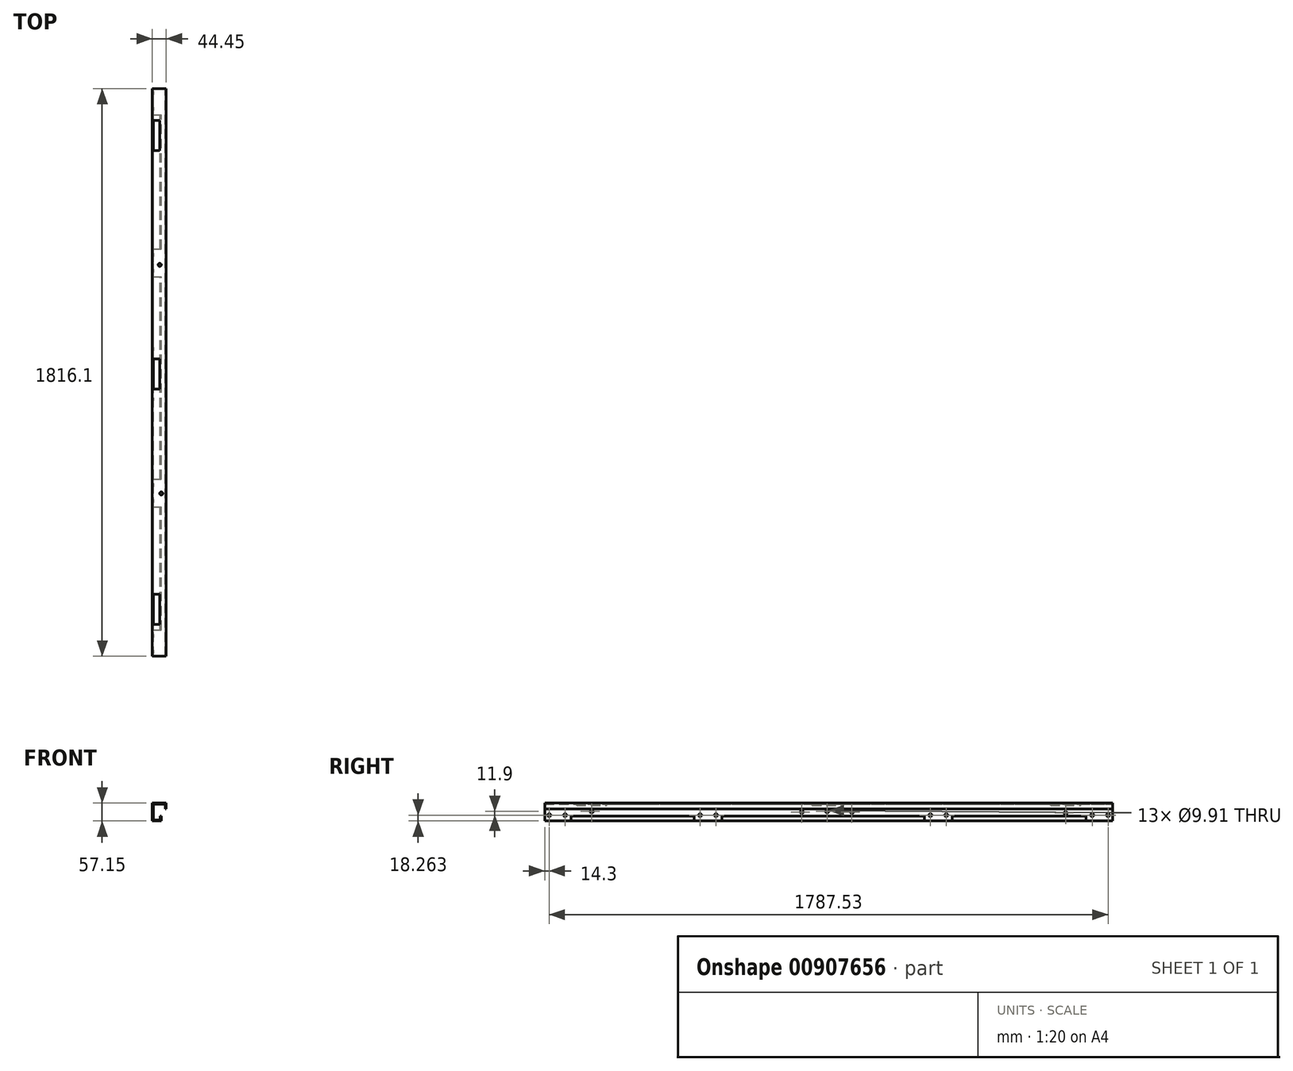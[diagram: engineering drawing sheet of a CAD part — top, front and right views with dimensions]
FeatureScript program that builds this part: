
annotation { "Feature Type Name" : "Feature", "Feature Type Description" : "" }
export const myFeature = defineFeature(function(context is Context, id is Id, definition is map)
    precondition{}
    {
        {
            var Q0;
            Q0=qCreatedBy(makeId("Front.planeOp"),FACE);
            var sketch = newSketch(context, id + "F0", { "sketchPlane" : qUnion([Q0])});
            skLineSegment(sketch, "E0", {"start": v(0, 0) * mm, "end": v(44.45, 0) * mm});
            skLineSegment(sketch, "E1", {"start": v(44.45, 0) * mm, "end": v(44.45, -19.05) * mm});
            skLineSegment(sketch, "E2", {"start": v(0, 0) * mm, "end": v(0, -57.15) * mm});
            skLineSegment(sketch, "E3", {"start": v(0, -57.15) * mm, "end": v(28.58, -57.15) * mm});
            skLineSegment(sketch, "E4", {"start": v(3.3, -53.85) * mm, "end": v(3.3, -3.3) * mm});
            skLineSegment(sketch, "E5", {"start": v(3.3, -3.3) * mm, "end": v(41.15, -3.3) * mm});
            skLineSegment(sketch, "E6", {"start": v(41.15, -3.3) * mm, "end": v(41.15, -19.05) * mm});
            skLineSegment(sketch, "E7", {"start": v(44.45, -19.05) * mm, "end": v(41.15, -19.05) * mm});
            skLineSegment(sketch, "E8", {"start": v(28.58, -41.27) * mm, "end": v(28.58, -57.15) * mm});
            skLineSegment(sketch, "E9", {"start": v(28.58, -41.27) * mm, "end": v(25.27, -41.27) * mm});
            skLineSegment(sketch, "E10", {"start": v(25.27, -41.27) * mm, "end": v(25.27, -53.85) * mm});
            skLineSegment(sketch, "E11", {"start": v(25.27, -53.85) * mm, "end": v(3.3, -53.85) * mm});
            skSolve(sketch);
        }
        {
            var Q0;
            Q0 = qSketchRegion(id + "F0", true);
            extrude(context, id + "F1", {"entities" : qUnion([Q0]), "depth" : 1816.1 * mm, "offsetDistance" : 25.4 * mm});
        }
        {
            var Q0;
            Q0=makeQuery(id+"F1.opExtrude","SWEPT_FACE",FACE,{"disambiguationData":[OSD([sQuery(id+"F0.wireOp",EDGE,"E0")])]});
            var sketch = newSketch(context, id + "F2", { "sketchPlane" : qUnion([Q0])});
            skCircle(sketch, "E12", {"center": v(23.62, -563.75) * mm, "radius": 4.95 * mm});
            skCircle(sketch, "E13", {"center": v(28.58, -1295.4) * mm, "radius": 4.97 * mm});
            skSolve(sketch);
        }
        {
            var Q0;
            Q0 = qSketchRegion(id + "F2", true);
            extrude(context, id + "F3", {"entities" : qUnion([Q0]), "operationType" : NewBodyOperationType.REMOVE, "oppositeDirection" : true, "depth" : 25.4 * mm, "offsetDistance" : 25.4 * mm});
        }
        {
            var Q0;
            Q0=makeQuery(id+"F1.opExtrude","SWEPT_FACE",FACE,{"disambiguationData":[OSD([sQuery(id+"F0.wireOp",EDGE,"E2")])]});
            var sketch = newSketch(context, id + "F4", { "sketchPlane" : qUnion([Q0])});
            skCircle(sketch, "E14", {"center": v(14.27, -38.89) * mm, "radius": 4.95 * mm});
            skCircle(sketch, "E15", {"center": v(65.07, -38.89) * mm, "radius": 4.95 * mm});
            skCircle(sketch, "E16", {"center": v(531.8, -38.89) * mm, "radius": 4.95 * mm});
            skCircle(sketch, "E17", {"center": v(582.6, -38.89) * mm, "radius": 4.95 * mm});
            skCircle(sketch, "E18", {"center": v(1268.4, -38.89) * mm, "radius": 4.95 * mm});
            skCircle(sketch, "E19", {"center": v(1319.2, -38.89) * mm, "radius": 4.95 * mm});
            skCircle(sketch, "E20", {"center": v(1751, -38.89) * mm, "radius": 4.95 * mm});
            skCircle(sketch, "E21", {"center": v(1801.8, -38.89) * mm, "radius": 4.95 * mm});
            skSolve(sketch);
        }
        {
            var Q0;
            Q0 = qSketchRegion(id + "F4", true);
            extrude(context, id + "F5", {"entities" : qUnion([Q0]), "operationType" : NewBodyOperationType.REMOVE, "oppositeDirection" : true, "depth" : 25.4 * mm, "offsetDistance" : 25.4 * mm});
        }
        {
            var Q0;
            Q0=makeQuery(id+"F1.opExtrude","SWEPT_FACE",FACE,{"disambiguationData":[OSD([sQuery(id+"F0.wireOp",EDGE,"E2")])]});
            var sketch = newSketch(context, id + "F6", { "sketchPlane" : qUnion([Q0])});
            skCircle(sketch, "E22", {"center": v(833.44, -28.58) * mm, "radius": 4.95 * mm});
            skCircle(sketch, "E23", {"center": v(993.78, -28.58) * mm, "radius": 4.95 * mm});
            skSolve(sketch);
        }
        {
            var Q0;
            Q0 = qSketchRegion(id + "F6", true);
            extrude(context, id + "F7", {"entities" : qUnion([Q0]), "operationType" : NewBodyOperationType.REMOVE, "oppositeDirection" : true, "depth" : 25.4 * mm, "offsetDistance" : 25.4 * mm});
        }
        {
            var Q0;
            Q0=makeQuery(id+"F1.opExtrude","SWEPT_FACE",FACE,{"disambiguationData":[OSD([sQuery(id+"F0.wireOp",EDGE,"E0")])]});
            var sketch = newSketch(context, id + "F8", { "sketchPlane" : qUnion([Q0])});
            skLineSegment(sketch, "E24.bottom", {"start": v(0, -101.6) * mm, "end": v(23.93, -101.6) * mm});
            skLineSegment(sketch, "E24.top", {"start": v(0, -198.44) * mm, "end": v(23.93, -198.44) * mm});
            skLineSegment(sketch, "E24.left", {"start": v(0, -101.6) * mm, "end": v(0, -198.44) * mm});
            skLineSegment(sketch, "E24.right", {"start": v(23.93, -101.6) * mm, "end": v(23.93, -198.44) * mm});
            skLineSegment(sketch, "E25.bottom", {"start": v(0, -1714.5) * mm, "end": v(24.13, -1714.5) * mm});
            skLineSegment(sketch, "E25.top", {"start": v(0, -1617.66) * mm, "end": v(24.13, -1617.66) * mm});
            skLineSegment(sketch, "E25.left", {"start": v(0, -1714.5) * mm, "end": v(0, -1617.66) * mm});
            skLineSegment(sketch, "E25.right", {"start": v(24.13, -1714.5) * mm, "end": v(24.13, -1617.66) * mm});
            skLineSegment(sketch, "E26.bottom", {"start": v(0, -961.22) * mm, "end": v(24.13, -961.22) * mm});
            skLineSegment(sketch, "E26.top", {"start": v(0, -864.39) * mm, "end": v(24.13, -864.39) * mm});
            skLineSegment(sketch, "E26.left", {"start": v(0, -961.22) * mm, "end": v(0, -864.39) * mm});
            skLineSegment(sketch, "E26.right", {"start": v(24.13, -961.22) * mm, "end": v(24.13, -864.39) * mm});
            skSolve(sketch);
        }
        {
            var Q0;
            Q0 = qSketchRegion(id + "F8", true);
            extrude(context, id + "F9", {"entities" : qUnion([Q0]), "operationType" : NewBodyOperationType.REMOVE, "oppositeDirection" : true, "depth" : 7.62 * mm, "offsetDistance" : 25.4 * mm});
        }
        {
            var Q0;
            Q0=makeQuery(id+"F1.opExtrude","SWEPT_FACE",FACE,{"disambiguationData":[OSD([sQuery(id+"F0.wireOp",EDGE,"E2")])]});
            var sketch = newSketch(context, id + "F10", { "sketchPlane" : qUnion([Q0])});
            skCircle(sketch, "E27", {"center": v(150.03, -31.94) * mm, "radius": 4.95 * mm});
            skCircle(sketch, "E28", {"center": v(912.81, -26.99) * mm, "radius": 4.95 * mm});
            skCircle(sketch, "E29", {"center": v(1666.09, -26.99) * mm, "radius": 4.95 * mm});
            skSolve(sketch);
        }
        {
            var Q0;
            Q0 = qSketchRegion(id + "F10", true);
            extrude(context, id + "F11", {"entities" : qUnion([Q0]), "operationType" : NewBodyOperationType.REMOVE, "oppositeDirection" : true, "depth" : 25.4 * mm, "offsetDistance" : 25.4 * mm});
        }
        {
            var Q0;
            Q0=makeQuery(id+"F1.opExtrude","SWEPT_FACE",FACE,{"disambiguationData":[OSD([sQuery(id+"F0.wireOp",EDGE,"E8")])]});
            var sketch = newSketch(context, id + "F12", { "sketchPlane" : qUnion([Q0])});
            skLineSegment(sketch, "E30.bottom", {"start": v(-1816.1, -57.15) * mm, "end": v(-1731.95, -57.15) * mm});
            skLineSegment(sketch, "E30.top", {"start": v(-1816.1, -41.27) * mm, "end": v(-1731.95, -41.27) * mm});
            skLineSegment(sketch, "E30.left", {"start": v(-1816.1, -57.15) * mm, "end": v(-1816.1, -41.27) * mm});
            skLineSegment(sketch, "E30.right", {"start": v(-1731.95, -57.15) * mm, "end": v(-1731.95, -41.27) * mm});
            skLineSegment(sketch, "E31.bottom", {"start": v(-1338.25, -57.15) * mm, "end": v(-1249.35, -57.15) * mm});
            skLineSegment(sketch, "E31.top", {"start": v(-1338.25, -41.28) * mm, "end": v(-1249.35, -41.28) * mm});
            skLineSegment(sketch, "E31.left", {"start": v(-1338.25, -57.15) * mm, "end": v(-1338.25, -41.28) * mm});
            skLineSegment(sketch, "E31.right", {"start": v(-1249.35, -57.15) * mm, "end": v(-1249.35, -41.28) * mm});
            skLineSegment(sketch, "E32.bottom", {"start": v(-601.65, -57.15) * mm, "end": v(-512.75, -57.15) * mm});
            skLineSegment(sketch, "E32.top", {"start": v(-601.65, -41.28) * mm, "end": v(-512.75, -41.28) * mm});
            skLineSegment(sketch, "E32.left", {"start": v(-601.65, -57.15) * mm, "end": v(-601.65, -41.28) * mm});
            skLineSegment(sketch, "E32.right", {"start": v(-512.75, -57.15) * mm, "end": v(-512.75, -41.28) * mm});
            skLineSegment(sketch, "E33.bottom", {"start": v(0, -57.15) * mm, "end": v(-84.12, -57.15) * mm});
            skLineSegment(sketch, "E33.top", {"start": v(0, -41.28) * mm, "end": v(-84.12, -41.28) * mm});
            skLineSegment(sketch, "E33.left", {"start": v(0, -57.15) * mm, "end": v(0, -41.28) * mm});
            skLineSegment(sketch, "E33.right", {"start": v(-84.12, -57.15) * mm, "end": v(-84.12, -41.28) * mm});
            skSolve(sketch);
        }
        {
            var Q0;
            Q0 = qSketchRegion(id + "F12", true);
            var Q1;
            Q1=makeQuery(id+"F1.opExtrude","SWEPT_FACE",FACE,{"disambiguationData":[OSD([sQuery(id+"F0.wireOp",EDGE,"E4")])]});
            extrude(context, id + "F13", {"entities" : qUnion([Q0]), "operationType" : NewBodyOperationType.REMOVE, "endBound" : BoundingType.UP_TO_SURFACE, "oppositeDirection" : true, "depth" : 25.4 * mm, "endBoundEntityFace" : qUnion([Q1]), "offsetDistance" : 25.4 * mm});
        }
    });
